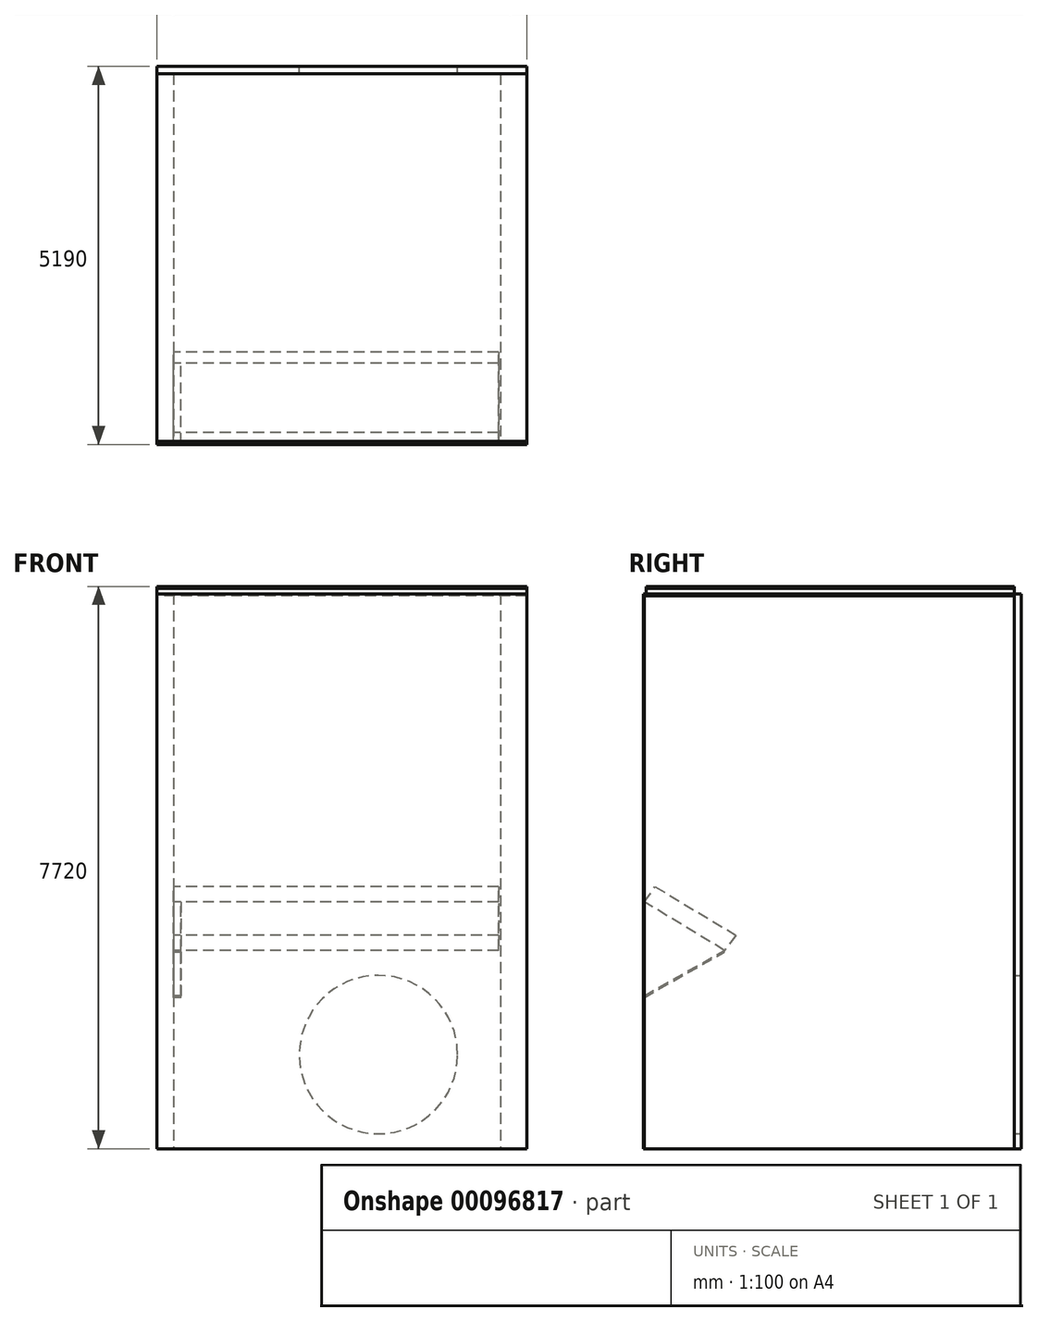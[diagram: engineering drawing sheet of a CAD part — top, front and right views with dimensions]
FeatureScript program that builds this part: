
annotation { "Feature Type Name" : "Feature", "Feature Type Description" : "" }
export const myFeature = defineFeature(function(context is Context, id is Id, definition is map)
    precondition{}
    {
        {
            var Q0;
            Q0=qCreatedBy(makeId("Front.planeOp"),FACE);
            var sketch = newSketch(context, id + "F0", { "sketchPlane" : qUnion([Q0])});
            skLineSegment(sketch, "E0.bottom", {"start": v(0, 0) * mm, "end": v(5080, 0) * mm});
            skLineSegment(sketch, "E0.top", {"start": v(0, 7620) * mm, "end": v(5080, 7620) * mm});
            skLineSegment(sketch, "E0.left", {"start": v(0, 0) * mm, "end": v(0, 7620) * mm});
            skLineSegment(sketch, "E0.right", {"start": v(5080, 0) * mm, "end": v(5080, 7620) * mm});
            skSolve(sketch);
        }
        {
            var Q0;
            Q0 = qSketchRegion(id + "F0", true);
            extrude(context, id + "F1", {"entities" : qUnion([Q0]), "depth" : 10 * mm});
        }
        {
            var Q0;
            Q0=makeQuery(id+"F1.opExtrude","CAP_FACE",FACE,{"disambiguationData":[OSD([sQuery(id+"F0.wireOp",EDGE,"E0.bottom"),sQuery(id+"F0.wireOp",EDGE,"E0.top"),sQuery(id+"F0.wireOp",EDGE,"E0.left"),sQuery(id+"F0.wireOp",EDGE,"E0.right")])],"isStart":true});
            var sketch = newSketch(context, id + "F2", { "sketchPlane" : qUnion([Q0])});
            skLineSegment(sketch, "E1.bottom", {"start": v(0, 7620) * mm, "end": v(-228.6, 7620) * mm});
            skLineSegment(sketch, "E1.top", {"start": v(0, 0) * mm, "end": v(-228.6, 0) * mm});
            skLineSegment(sketch, "E1.left", {"start": v(0, 7620) * mm, "end": v(0, 0) * mm});
            skLineSegment(sketch, "E1.right", {"start": v(-228.6, 7620) * mm, "end": v(-228.6, 0) * mm});
            skSolve(sketch);
        }
        {
            var Q0;
            Q0 = qSketchRegion(id + "F2", true);
            var Q1;
            Q1 = qSketchRegion(id + "F4", true);
            var Q2;
            Q2 = qSketchRegion(id + "F8", true);
            extrude(context, id + "F3", {"entities" : qUnion([Q0, Q1, Q2]), "depth" : 5080 * mm});
        }
        {
            var Q0;
            Q0=makeQuery(id+"F3.opExtrude","SWEPT_FACE",FACE,{"disambiguationData":[OSD([sQuery(id+"F2.wireOp",EDGE,"E1.right")])]});
            var sketch = newSketch(context, id + "F4", { "sketchPlane" : qUnion([Q0])});
            skLineSegment(sketch, "E2", {"start": v(0, 3390.58) * mm, "end": v(0, 2100.93) * mm});
            skLineSegment(sketch, "E3", {"start": v(-1.67, 2099.99) * mm, "end": v(1103.18, 2723.7) * mm});
            skLineSegment(sketch, "E4", {"start": v(1103.18, 2723.7) * mm, "end": v(0, 3390.58) * mm});
            skSolve(sketch);
        }
        {
            var Q0;
            Q0 = qSketchRegion(id + "F4", true);
            extrude(context, id + "F5", {"entities" : qUnion([Q0]), "depth" : 100 * mm});
        }
        {
            var Q0;
            Q0=makeQuery(id+"F3.opExtrude","SWEPT_FACE",FACE,{"disambiguationData":[OSD([sQuery(id+"F2.wireOp",EDGE,"E1.right")])]});
            var sketch = newSketch(context, id + "F6", { "sketchPlane" : qUnion([Q0])});
            skLineSegment(sketch, "E5", {"start": v(1103.18, 2723.7) * mm, "end": v(0, 3390.58) * mm});
            skLineSegment(sketch, "E6", {"start": v(0, 3390.58) * mm, "end": v(152.02, 3596.54) * mm});
            skLineSegment(sketch, "E7", {"start": v(152.02, 3596.54) * mm, "end": v(1257.57, 2932.85) * mm});
            skLineSegment(sketch, "E8", {"start": v(1257.57, 2932.85) * mm, "end": v(1103.18, 2723.7) * mm});
            skSolve(sketch);
        }
        {
            var Q0;
            Q0=makeQuery(id+"F6.imprint","IMPRINT",FACE,{"disambiguationData":[TD([[makeQuery(id+"F6.imprint","IMPRINT",EDGE,{"derivedFrom":sQuery(id+"F6.wireOp",EDGE,"E5")}),-1.0]])]});
            extrude(context, id + "F7", {"entities" : qUnion([Q0]), "depth" : 4464.55 * mm});
        }
        {
            var Q0;
            Q0=makeQuery(id+"F1.opExtrude","CAP_FACE",FACE,{"disambiguationData":[OSD([sQuery(id+"F0.wireOp",EDGE,"E0.bottom"),sQuery(id+"F0.wireOp",EDGE,"E0.top"),sQuery(id+"F0.wireOp",EDGE,"E0.left"),sQuery(id+"F0.wireOp",EDGE,"E0.right")])],"isStart":true});
            var sketch = newSketch(context, id + "F8", { "sketchPlane" : qUnion([Q0])});
            skLineSegment(sketch, "E9.bottom", {"start": v(-5080, 7620) * mm, "end": v(-4719.91, 7620) * mm});
            skLineSegment(sketch, "E9.top", {"start": v(-5080, 0) * mm, "end": v(-4719.91, 0) * mm});
            skLineSegment(sketch, "E9.left", {"start": v(-5080, 7620) * mm, "end": v(-5080, 0) * mm});
            skLineSegment(sketch, "E9.right", {"start": v(-4719.91, 7620) * mm, "end": v(-4719.91, 0) * mm});
            skSolve(sketch);
        }
        {
            var Q0;
            Q0=makeQuery(id+"F8.imprint","IMPRINT",FACE,{"disambiguationData":[TD([[makeQuery(id+"F8.imprint","IMPRINT",EDGE,{"derivedFrom":sQuery(id+"F8.wireOp",EDGE,"E9.bottom")}),1.0]])]});
            extrude(context, id + "F9", {"entities" : qUnion([Q0]), "depth" : 5080 * mm});
        }
        {
            var Q0;
            Q0=makeQuery(id+"F9.opExtrude","CAP_FACE",FACE,{"disambiguationData":[OSD([sQuery(id+"F8.wireOp",EDGE,"E9.bottom"),sQuery(id+"F8.wireOp",EDGE,"E9.top"),sQuery(id+"F8.wireOp",EDGE,"E9.left"),sQuery(id+"F8.wireOp",EDGE,"E9.right")])],"isStart":false});
            var sketch = newSketch(context, id + "F10", { "sketchPlane" : qUnion([Q0])});
            skLineSegment(sketch, "E10.bottom", {"start": v(-5080, 7620) * mm, "end": v(0, 7620) * mm});
            skLineSegment(sketch, "E10.top", {"start": v(-5080, 0) * mm, "end": v(0, 0) * mm});
            skLineSegment(sketch, "E10.left", {"start": v(-5080, 7620) * mm, "end": v(-5080, 0) * mm});
            skLineSegment(sketch, "E10.right", {"start": v(0, 7620) * mm, "end": v(0, 0) * mm});
            skSolve(sketch);
        }
        {
            var Q0;
            Q0 = qSketchRegion(id + "F10", true);
            extrude(context, id + "F11", {"entities" : qUnion([Q0]), "depth" : 100 * mm});
        }
        {
            var Q0;
            Q0=makeQuery(id+"F11.opExtrude","SWEPT_FACE",FACE,{"disambiguationData":[OSD([sQuery(id+"F10.wireOp",EDGE,"E10.bottom")])]});
            var sketch = newSketch(context, id + "F12", { "sketchPlane" : qUnion([Q0])});
            skLineSegment(sketch, "E11.bottom", {"start": v(0, 30.43) * mm, "end": v(5080, 30.43) * mm});
            skLineSegment(sketch, "E11.top", {"start": v(0, 5180) * mm, "end": v(5080, 5180) * mm});
            skLineSegment(sketch, "E11.left", {"start": v(0, 30.43) * mm, "end": v(0, 5180) * mm});
            skLineSegment(sketch, "E11.right", {"start": v(5080, 30.43) * mm, "end": v(5080, 5180) * mm});
            skSolve(sketch);
        }
        {
            var Q0;
            {var subQ0=sQuery(id+"F12.wireOp",EDGE,"E11.bottom");Q0=makeQuery(id+"F12.imprint","IMPRINT",FACE,{"disambiguationData":[TD([[makeQuery(id+"F12.imprint","IMPRINT",EDGE,{"derivedFrom":subQ0}),1.0]])]});}
            extrude(context, id + "F13", {"entities" : qUnion([Q0]), "depth" : 100 * mm});
        }
        {
            var Q0;
            Q0=makeQuery(id+"F11.opExtrude","CAP_FACE",FACE,{"disambiguationData":[OSD([sQuery(id+"F10.wireOp",EDGE,"E10.bottom"),sQuery(id+"F10.wireOp",EDGE,"E10.top"),sQuery(id+"F10.wireOp",EDGE,"E10.left"),sQuery(id+"F10.wireOp",EDGE,"E10.right")])],"isStart":false});
            var sketch = newSketch(context, id + "F14", { "sketchPlane" : qUnion([Q0])});
            skCircle(sketch, "E12", {"center": v(-3042.37, 1291.88) * mm, "radius": 1087.5 * mm});
            skSolve(sketch);
        }
        {
            var Q0;
            Q0 = qSketchRegion(id + "F14", true);
            extrude(context, id + "F15", {"entities" : qUnion([Q0]), "operationType" : NewBodyOperationType.REMOVE, "oppositeDirection" : true, "depth" : 999 * mm});
        }
        {
            var Q0;
            Q0=makeQuery(id+"F13.opExtrude","CAP_FACE",FACE,{"disambiguationData":[OSD([sQuery(id+"F10.wireOp",EDGE,"E10.bottom"),sQuery(id+"F12.wireOp",EDGE,"E11.bottom"),sQuery(id+"F12.wireOp",EDGE,"E11.left"),sQuery(id+"F12.wireOp",EDGE,"E11.right")])],"isStart":true});
            var sketch = newSketch(context, id + "F16", { "sketchPlane" : qUnion([Q0])});
            skSolve(sketch);
        }
        {
            var Q0;
            Q0=makeQuery(id+"F16.imprint","IMPRINT",FACE,{"disambiguationData":[TD([[makeQuery(id+"F16.imprint","IMPRINT",EDGE,{"derivedFrom":makeQuery(id+"F13.opExtrude","CAP_EDGE",EDGE,{"disambiguationData":[OSD([sQuery(id+"F12.wireOp",EDGE,"E11.bottom")])],"isStart":true})}),-1.0]])]});
            var Q1;
            Q1=makeQuery(id+"F13.opExtrude","CAP_FACE",FACE,{"disambiguationData":[OSD([sQuery(id+"F10.wireOp",EDGE,"E10.bottom"),sQuery(id+"F12.wireOp",EDGE,"E11.bottom"),sQuery(id+"F12.wireOp",EDGE,"E11.left"),sQuery(id+"F12.wireOp",EDGE,"E11.right")])],"isStart":true});
            var Q2;
            Q2=makeQuery(id+"F13.opExtrude","CAP_FACE",FACE,{"disambiguationData":[OSD([sQuery(id+"F10.wireOp",EDGE,"E10.bottom"),sQuery(id+"F12.wireOp",EDGE,"E11.bottom"),sQuery(id+"F12.wireOp",EDGE,"E11.left"),sQuery(id+"F12.wireOp",EDGE,"E11.right")])],"isStart":false});
            var Q3;
            Q3=makeQuery(id+"F5.opExtrude","SWEPT_FACE",FACE,{"disambiguationData":[OSD([sQuery(id+"F4.wireOp",EDGE,"E3")])]});
            extrude(context, id + "F17", {"entities" : qUnion([Q0, Q1, Q2, Q3]), "depth" : 25 * mm});
        }
    });
